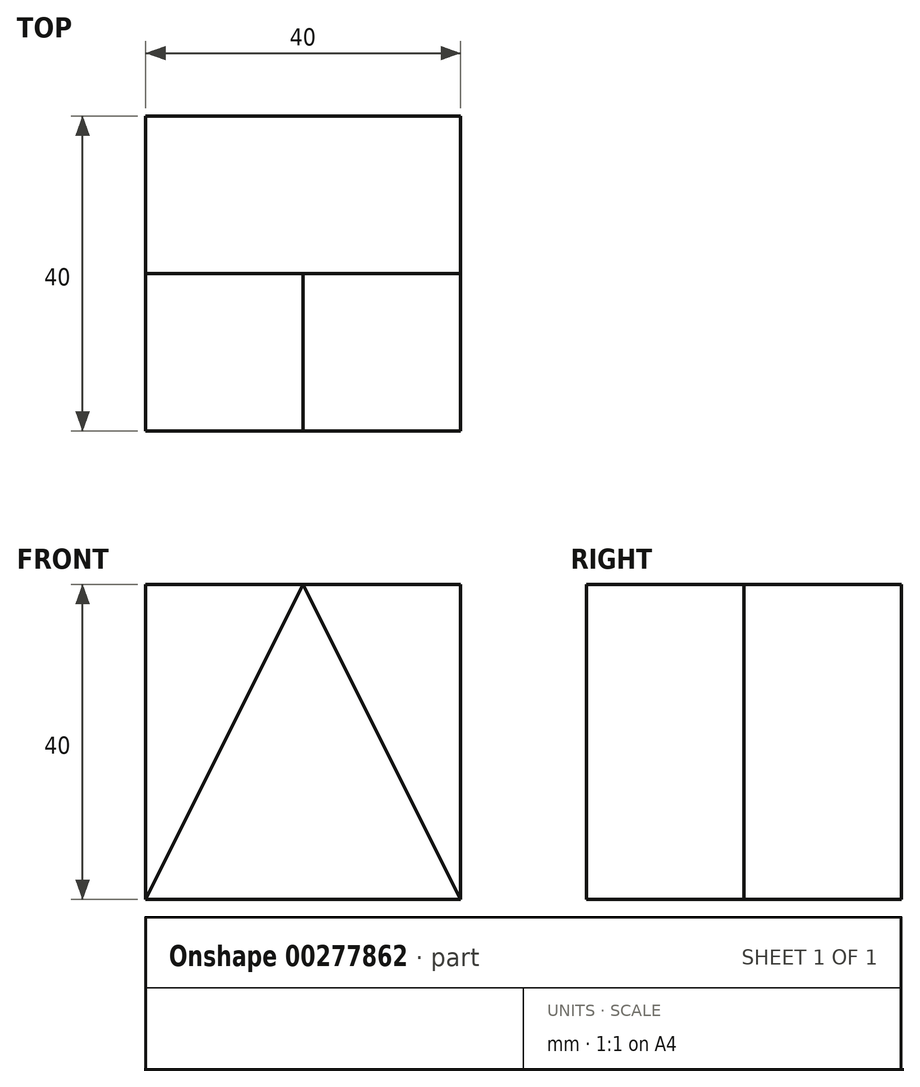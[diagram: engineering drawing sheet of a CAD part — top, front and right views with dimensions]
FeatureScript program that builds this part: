
annotation { "Feature Type Name" : "Feature", "Feature Type Description" : "" }
export const myFeature = defineFeature(function(context is Context, id is Id, definition is map)
    precondition{}
    {
        {
            var Q0;
            Q0=qCreatedBy(makeId("Front.planeOp"),FACE);
            var sketch = newSketch(context, id + "F0", { "sketchPlane" : qUnion([Q0])});
            skLineSegment(sketch, "E0.bottom", {"start": v(0, 0) * mm, "end": v(40, 0) * mm});
            skLineSegment(sketch, "E0.top", {"start": v(0, 40) * mm, "end": v(40, 40) * mm});
            skLineSegment(sketch, "E0.left", {"start": v(0, 0) * mm, "end": v(0, 40) * mm});
            skLineSegment(sketch, "E0.right", {"start": v(40, 0) * mm, "end": v(40, 40) * mm});
            skSolve(sketch);
        }
        {
            var Q0;
            Q0 = qSketchRegion(id + "F0", true);
            extrude(context, id + "F1", {"entities" : qUnion([Q0]), "depth" : 20 * mm});
        }
        {
            var Q0;
            Q0=makeQuery(id+"F1.opExtrude","CAP_FACE",FACE,{"disambiguationData":[OSD([sQuery(id+"F0.wireOp",EDGE,"E0.bottom"),sQuery(id+"F0.wireOp",EDGE,"E0.top"),sQuery(id+"F0.wireOp",EDGE,"E0.left"),sQuery(id+"F0.wireOp",EDGE,"E0.right")])],"isStart":false});
            var sketch = newSketch(context, id + "F2", { "sketchPlane" : qUnion([Q0])});
            skLineSegment(sketch, "E1.0", {"start": v(0, 0) * mm, "end": v(40, 0) * mm});
            skLineSegment(sketch, "E2", {"start": v(0, 0) * mm, "end": v(20, 40) * mm});
            skLineSegment(sketch, "E3", {"start": v(20, 40) * mm, "end": v(40, 0) * mm});
            skSolve(sketch);
        }
        {
            var Q0;
            Q0 = qSketchRegion(id + "F2", true);
            extrude(context, id + "F3", {"entities" : qUnion([Q0]), "operationType" : NewBodyOperationType.ADD, "depth" : 20 * mm});
        }
    });
